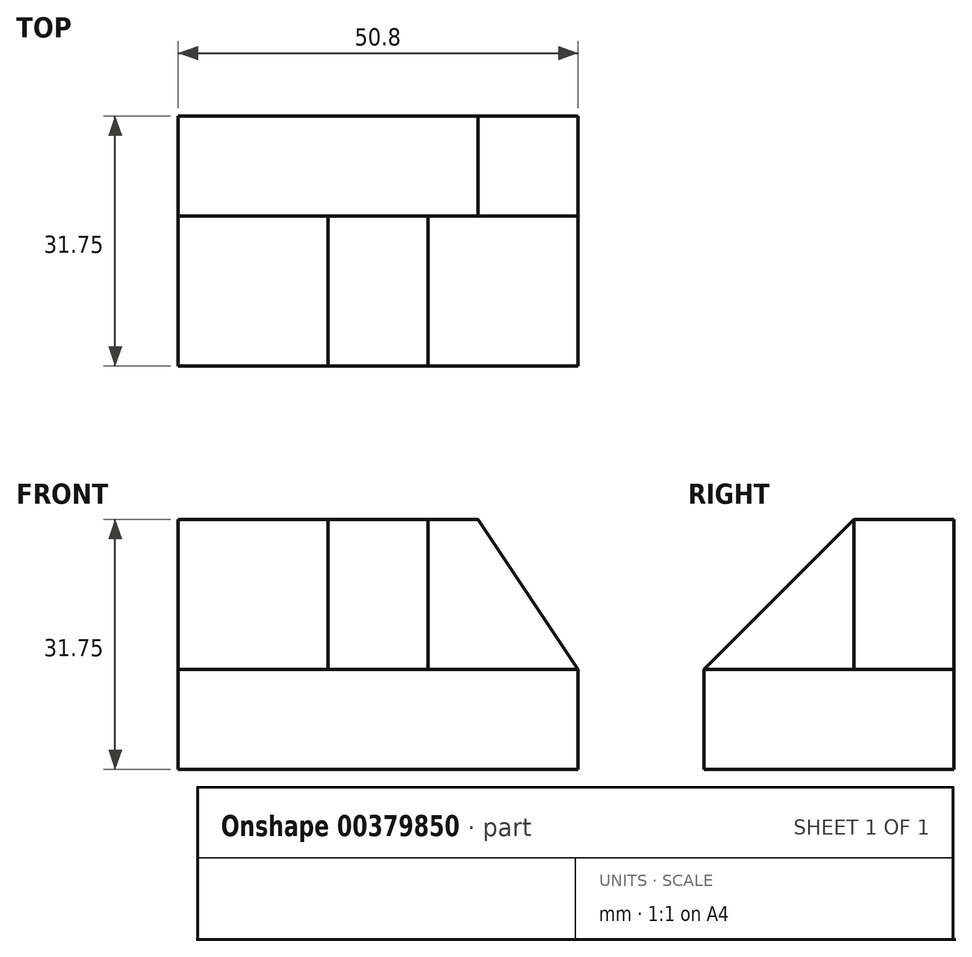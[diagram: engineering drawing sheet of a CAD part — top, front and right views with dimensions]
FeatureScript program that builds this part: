
annotation { "Feature Type Name" : "Feature", "Feature Type Description" : "" }
export const myFeature = defineFeature(function(context is Context, id is Id, definition is map)
    precondition{}
    {
        {
            var Q0;
            Q0=qCreatedBy(makeId("Right.planeOp"),FACE);
            var sketch = newSketch(context, id + "F0", { "sketchPlane" : qUnion([Q0])});
            skLineSegment(sketch, "E0", {"start": v(0, 0) * mm, "end": v(0, 12.7) * mm});
            skLineSegment(sketch, "E1", {"start": v(0, 12.7) * mm, "end": v(19.05, 12.7) * mm});
            skLineSegment(sketch, "E2", {"start": v(19.05, 12.7) * mm, "end": v(19.05, 31.75) * mm});
            skLineSegment(sketch, "E3", {"start": v(19.05, 31.75) * mm, "end": v(31.75, 31.75) * mm});
            skLineSegment(sketch, "E4", {"start": v(31.75, 31.75) * mm, "end": v(31.75, 0) * mm});
            skLineSegment(sketch, "E5", {"start": v(31.75, 0) * mm, "end": v(0, 0) * mm});
            skSolve(sketch);
        }
        {
            var Q0;
            Q0 = qSketchRegion(id + "F0", true);
            extrude(context, id + "F1", {"entities" : qUnion([Q0]), "depth" : 50.8 * mm});
        }
        {
            var Q0;
            Q0=makeQuery(id+"F1.opExtrude","SWEPT_FACE",FACE,{"disambiguationData":[OSD([sQuery(id+"F0.wireOp",EDGE,"E2")])]});
            var sketch = newSketch(context, id + "F2", { "sketchPlane" : qUnion([Q0])});
            skLineSegment(sketch, "E6", {"start": v(0, 31.75) * mm, "end": v(38.1, 31.75) * mm});
            skLineSegment(sketch, "E7", {"start": v(38.1, 31.75) * mm, "end": v(50.8, 12.7) * mm});
            skSolve(sketch);
        }
        {
            var Q0;
            Q0 = qSketchRegion(id + "F2", true);
            var Q1;
            {var subQ0=sQuery(id+"F2.wireOp",EDGE,"E7");Q1=makeQuery(id+"F2.imprint","IMPRINT",FACE,{"disambiguationData":[TD([[makeQuery(id+"F2.imprint","IMPRINT",EDGE,{"derivedFrom":subQ0}),1.0]])]});}
            extrude(context, id + "F3", {"entities" : qUnion([Q0, Q1]), "operationType" : NewBodyOperationType.REMOVE, "oppositeDirection" : true, "depth" : 25.4 * mm});
        }
        {
            var Q0;
            Q0=makeQuery(id+"F1.opExtrude","CAP_FACE",FACE,{"disambiguationData":[OSD([sQuery(id+"F0.wireOp",EDGE,"E0"),sQuery(id+"F0.wireOp",EDGE,"E1"),sQuery(id+"F0.wireOp",EDGE,"E2"),sQuery(id+"F0.wireOp",EDGE,"E3"),sQuery(id+"F0.wireOp",EDGE,"E4"),sQuery(id+"F0.wireOp",EDGE,"E5")])],"isStart":true});
            var sketch = newSketch(context, id + "F4", { "sketchPlane" : qUnion([Q0])});
            skLineSegment(sketch, "E8", {"start": v(0, 12.7) * mm, "end": v(-19.05, 31.75) * mm});
            skSolve(sketch);
        }
        {
            var Q0;
            Q0 = qSketchRegion(id + "F4", true);
            var Q1;
            Q1=makeQuery(id+"F4.imprint","IMPRINT",FACE,{"disambiguationData":[TD([[makeQuery(id+"F4.imprint","IMPRINT",EDGE,{"derivedFrom":sQuery(id+"F4.wireOp",EDGE,"E8")}),1.0]])]});
            extrude(context, id + "F5", {"entities" : qUnion([Q0, Q1]), "operationType" : NewBodyOperationType.ADD, "oppositeDirection" : true, "depth" : 31.75 * mm});
        }
        {
            var Q0;
            {var subQ0=sQuery(id+"F0.wireOp",EDGE,"E2");var subQ1=sQuery(id+"F0.wireOp",EDGE,"E1");Q0=makeQuery(id+"F5.boolean.opBoolean","MERGE",FACE,{"derivedFrom":[makeQuery(id+"F1.opExtrude","CAP_FACE",FACE,{"disambiguationData":[OSD([sQuery(id+"F0.wireOp",EDGE,"E0"),subQ1,subQ0,sQuery(id+"F0.wireOp",EDGE,"E3"),sQuery(id+"F0.wireOp",EDGE,"E4"),sQuery(id+"F0.wireOp",EDGE,"E5")])],"isStart":true}),makeQuery(id+"F5.opExtrude","CAP_FACE",FACE,{"disambiguationData":[OSD([subQ1,subQ0,sQuery(id+"F4.wireOp",EDGE,"E8")])],"isStart":true})]});}
            var sketch = newSketch(context, id + "F6", { "sketchPlane" : qUnion([Q0])});
            skLineSegment(sketch, "E9", {"start": v(0, 12.7) * mm, "end": v(-19.05, 12.7) * mm});
            skLineSegment(sketch, "E10", {"start": v(-19.05, 12.7) * mm, "end": v(-19.05, 31.75) * mm});
            skSolve(sketch);
        }
        {
            var Q0;
            Q0 = qSketchRegion(id + "F6", true);
            var Q1;
            Q1=makeQuery(id+"F6.imprint","IMPRINT",FACE,{"disambiguationData":[TD([[makeQuery(id+"F6.imprint","IMPRINT",EDGE,{"derivedFrom":sQuery(id+"F6.wireOp",EDGE,"E9")}),-1.0]])]});
            extrude(context, id + "F7", {"entities" : qUnion([Q0, Q1]), "operationType" : NewBodyOperationType.REMOVE, "oppositeDirection" : true, "depth" : 19.05 * mm});
        }
    });
